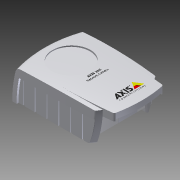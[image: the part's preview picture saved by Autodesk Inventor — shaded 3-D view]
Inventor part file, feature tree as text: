
AUTODESK INVENTOR PART (.ipt)
format: ipt  version: 2011 (Build 150239000, 239)  size: 4,475,904 bytes
history: native  units: in
note: dims shown in document units (in); Inventor stores cm internally (conversion verified against a paired STEP export)
features: extrude x38, sketch x37, plane x9, projected_geometry x9, revolve x6, fillet x5, loft x2, emboss x2, reference x1
ambient origin geometry x8: Origin, YZ Plane, XZ Plane, XY Plane, X Axis, Y Axis, Z Axis, Center Point
bodies: Solid1 (feature_tree)
feature tree (109):
  extrude  "Extrusion1"  Depth=3.0in
  sketch  "Sketch2"  dims[d2=2.175in d3=0.0in d5=1.0in]
  revolve  "Revolution1"  [1 undecoded]
  plane  "Work Plane1"
  sketch  "Sketch3"  dims[d6=90.0deg d7=-1.0875in]
  revolve  "Revolution2"  [1 undecoded]
  extrude  "Extrusion2"  Depth=0.0426in
  revolve  "Revolution3"  [1 undecoded]
  revolve  "Revolution4"  [1 undecoded]
  fillet  "Fillet1"  Radius=0.6875in
  revolve  "Revolution5"  [1 undecoded]
  fillet  "Fillet2"  Radius=2.0086in
  plane  "Work Plane2"
  revolve  "Revolution6"  [1 undecoded]
  sketch  "Sketch9"  dims[d17=0.6875in d18=0.035in d19=2.0086in]
  plane  "Work Plane4"
  extrude  "Extrusion3"  Depth=0.225in
  extrude  "Extrusion6"  Depth=0.15in
  plane  "Work Plane5"
  extrude  "Extrusion7"  Depth=0.2in
  sketch  "Sketch13"  dims[d26=0.225in d27=0.225in]
  sketch  "Sketch14"  dims[d28=0.15in d29=0.15in]
  loft  "Loft1"
  extrude  "Extrusion8"  Depth=0.275in
  loft  "Loft2"
  extrude  "Extrusion9"  TaperAngle=0.0deg  [1 undecoded]
  extrude  "Extrusion10"  Depth=3.7722in
  sketch  "Sketch19"  dims[d38=-0.875in d41=0.0in]
  sketch  "Sketch20"  dims[d42=0.25in d43=0.0in]
  extrude  "Extrusion13"  Depth=1.0in TaperAngle=0.0deg
  extrude  "Extrusion14"  Depth=0.085in TaperAngle=0.0deg
  extrude  "Extrusion15"  Depth=0.085in
  extrude  "Extrusion16"  Depth=0.3516in
  extrude  "Extrusion17"  Depth=0.075in
  extrude  "Extrusion18"  Depth=0.085in
  extrude  "Extrusion19"  TaperAngle=0.0deg  [1 undecoded]
  extrude  "Extrusion20"  Depth=0.085in
  extrude  "Extrusion21"  Depth=0.085in
  plane  "Work Plane7"
  plane  "Work Plane8"
  extrude  "Extrusion22"  TaperAngle=0.0deg  [1 undecoded]
  extrude  "Extrusion24"  Depth=1.0in TaperAngle=0.0deg
  extrude  "Extrusion25"  Depth=0.075in
  extrude  "Extrusion26"  Depth=0.75in
  extrude  "Extrusion27"  Depth=0.025in
  fillet  "Fillet3"  Radius=0.06in
  extrude  "Extrusion28"  Depth=2.3622in
  fillet  "Fillet4"  Radius=0.8in
  extrude  "Extrusion29"  Depth=0.15in
  sketch  "Sketch37"  dims[d91=0.075in d92=0.75in]
  fillet  "Fillet5"  Radius=0.005in
  extrude  "Extrusion30"  Depth=0.032in
  extrude  "Extrusion31"  Depth=0.75in TaperAngle=0.0deg
  plane  "Work Plane9"
  sketch  "Sketch39"  dims[d99=0.0in d101=2.3622in d103=0.4in d104=0.7874in d106=2.0in d111=0.8in d112=0.0in]
  extrude  "Extrusion32"  Depth=0.15in
  plane  "Work Plane10"
  sketch  "Sketch43"  dims[d126=0.75in d127=0.0in d130=0.15in]
  extrude  "Extrusion35"  Depth=0.75in TaperAngle=0.0deg
  extrude  "Extrusion36"  Depth=0.01in
  plane  "Work Plane11"
  sketch  "Sketch44"  dims[d131=0.2984in d132=0.75in d133=0.0in]
  extrude  "Extrusion37"  Depth=0.069in
  extrude  "Extrusion38"  Depth=0.01in
  extrude  "Extrusion39"  Depth=0.75in TaperAngle=0.0deg
  extrude  "Extrusion40"  Depth=0.75in TaperAngle=0.0deg
  extrude  "Extrusion41"  Depth=0.75in TaperAngle=0.0deg
  extrude  "Extrusion42"  Depth=40.6825in
  extrude  "Extrusion43"  Depth=1.4254in
  emboss  "Emboss1"
  emboss  "Emboss2"
  sketch  "Sketch1"  dims[d0=1.085in d1=3.0in]
  projected_geometry  "Projected Loop1"
  sketch  "Sketch5"  dims[d9=20.3413in d10=0.0426in]
  sketch  "Sketch6"  dims[d11=2.175in d12=0.0in d13=0.0426in]
  sketch  "Sketch8"  dims[d14=0.0426in d15=0.1825in d16=0.6875in]
  projected_geometry  "Projected Loop2"
  sketch  "Sketch12"  dims[d20=0.1718in d21=0.005in]
  projected_geometry  "Projected Loop7"
  sketch  "Sketch15"  dims[d30=0.1718in d32=0.2in]
  sketch  "Sketch16"  dims[d33=0.2in d34=1.9in]
  sketch  "Sketch17"  dims[d35=0.0277in d36=0.275in d37=8.0944in]
  sketch  "Sketch21"  dims[d44=0.25in d45=3.7722in]
  sketch  "Sketch22"  dims[d46=0.3987in d47=1.0in d48=0.0in]
  sketch  "Sketch23"  dims[d49=0.225in d56=0.085in d57=0.0in]
  projected_geometry  "Projected Loop8"
  sketch  "Sketch24"  dims[d58=-0.085in d59=0.085in]
  projected_geometry  "Projected Loop9"
  sketch  "Sketch25"  dims[d60=0.085in d61=0.3516in]
  projected_geometry  "Projected Loop10"
  sketch  "Sketch28"  dims[d65=0.085in d66=0.085in]
  projected_geometry  "Projected Loop12"
  sketch  "Sketch30"  dims[d67=0.0in d68=90.0deg d69=0.0in d70=90.0deg]
  projected_geometry  "Projected Loop14"
  sketch  "Sketch31"  dims[d71=0.085in d72=0.0in d73=0.085in]
  sketch  "Sketch32"  dims[d74=0.075in d76=0.085in]
  sketch  "Sketch33"  dims[d77=0.0in d78=90.0deg d79=0.0in d80=90.0deg]
  sketch  "Sketch34"  dims[d81=0.085in d82=0.0in d83=1.0in d84=0.0in]
  sketch  "Sketch36"  dims[d89=0.8883in d90=0.075in]
  sketch  "Sketch38"  dims[d94=0.0in d97=0.025in d98=0.06in]
  sketch  "Sketch40"  dims[d113=0.15in d114=0.15in d115=0.005in d116=0.0in]
  projected_geometry  "Projected Loop15"
  sketch  "Sketch41"  dims[d117=0.032in d118=0.032in]
  sketch  "Sketch42"  dims[d119=0.8in d120=0.0in d121=0.75in d122=0.0in]
  reference  "Reference1"
  sketch  "Sketch45"  dims[d134=0.069in d135=0.01in d136=0.069in d137=0.01in d138=0.75in d139=0.0in d140=0.75in d141=0.0in d142=0.75in d143=0.0in d148=40.6825in d149=0.05in d150=1.12in d159=1.4254in d162=1.3595in d163=1.85in d166=0.45in d167=1.0in d168=0.0in d171=1.0in d172=0.0in d173=1.0in d174=0.0in d175=1.0in d176=0.0in d177=0.1in d178=1.0in d179=0.0in d180=0.075in d181=0.06in d182=0.0in d183=0.0625in d184=0.05in d185=0.0in d186=0.125in d187=0.05in d188=0.0in d189=0.076in d190=0.175in d191=0.076in d192=0.121in d193=0.16in d194=0.16in d195=0.16in d198=0.0in d199=0.3985in d200=0.225in d201=0.05in d202=0.0in d203=1.25in d204=1.27in d205=0.975in d206=1.0in d207=0.0in d208=0.25in d209=0.65in d210=0.725in d212=0.0in d213=0.0025in d214=0.1in d215=0.1in d216=0.1748in d217=0.0in d218=0.05in d219=0.0in d220=0.33in d221=0.435in d222=0.5in d224=0.0in d225=0.48in d226=1.125in d227=0.21in d228=0.0in d229=0.4in d230=0.0in d242=0.0in d243=1.0in d244=0.0in d245=0.0in d246=0.0in d247=0.0in d257=0.0in d258=0.0in d259=0.0002in d260=0.0in d261=0.0in d262=0.0in d263=0.0in d264=0.0in d265=0.0in d266=0.0in d267=0.001in d268=0.0in d269=0.0in d270=1.2148in d271=0.001in d272=0.0in]
  sketch  "Sketch27"  dims[d62=0.085in d63=0.0in d64=0.075in]
  extrude  "Extrusion33"  Depth=1.3595in
  extrude  "Extrusion34"  Depth=1.85in
note: 9 required parameter values undecoded (feature->parameter linkage not recoverable at this tier; creation-order binding heuristic only, values carry confidence <= 0.55)